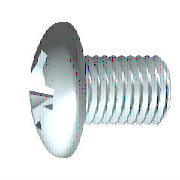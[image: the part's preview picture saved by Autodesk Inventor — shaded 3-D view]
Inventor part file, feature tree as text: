
AUTODESK INVENTOR PART (.ipt)
format: ipt  version: 2022 (Build 260153000, 153)  size: 337,408 bytes
history: native  units: mm (DEFAULTED — no unit token found)
features: other x2, plane x2, extrude x2
ambient origin geometry x7: Origin, YZ Plane, XZ Plane, X Axis, Y Axis, Z Axis, Center Point
bodies: Solid1 (feature_tree)
feature tree (6):
  other  "Базовый элемент"
  plane  "Work Plane1"
  extrude  "Паз"  Depth=4.0mm
  other  "Вырез"
  extrude  "Прорезь крестообразная"  Depth=2.34mm
  plane  "Work Plane3"
